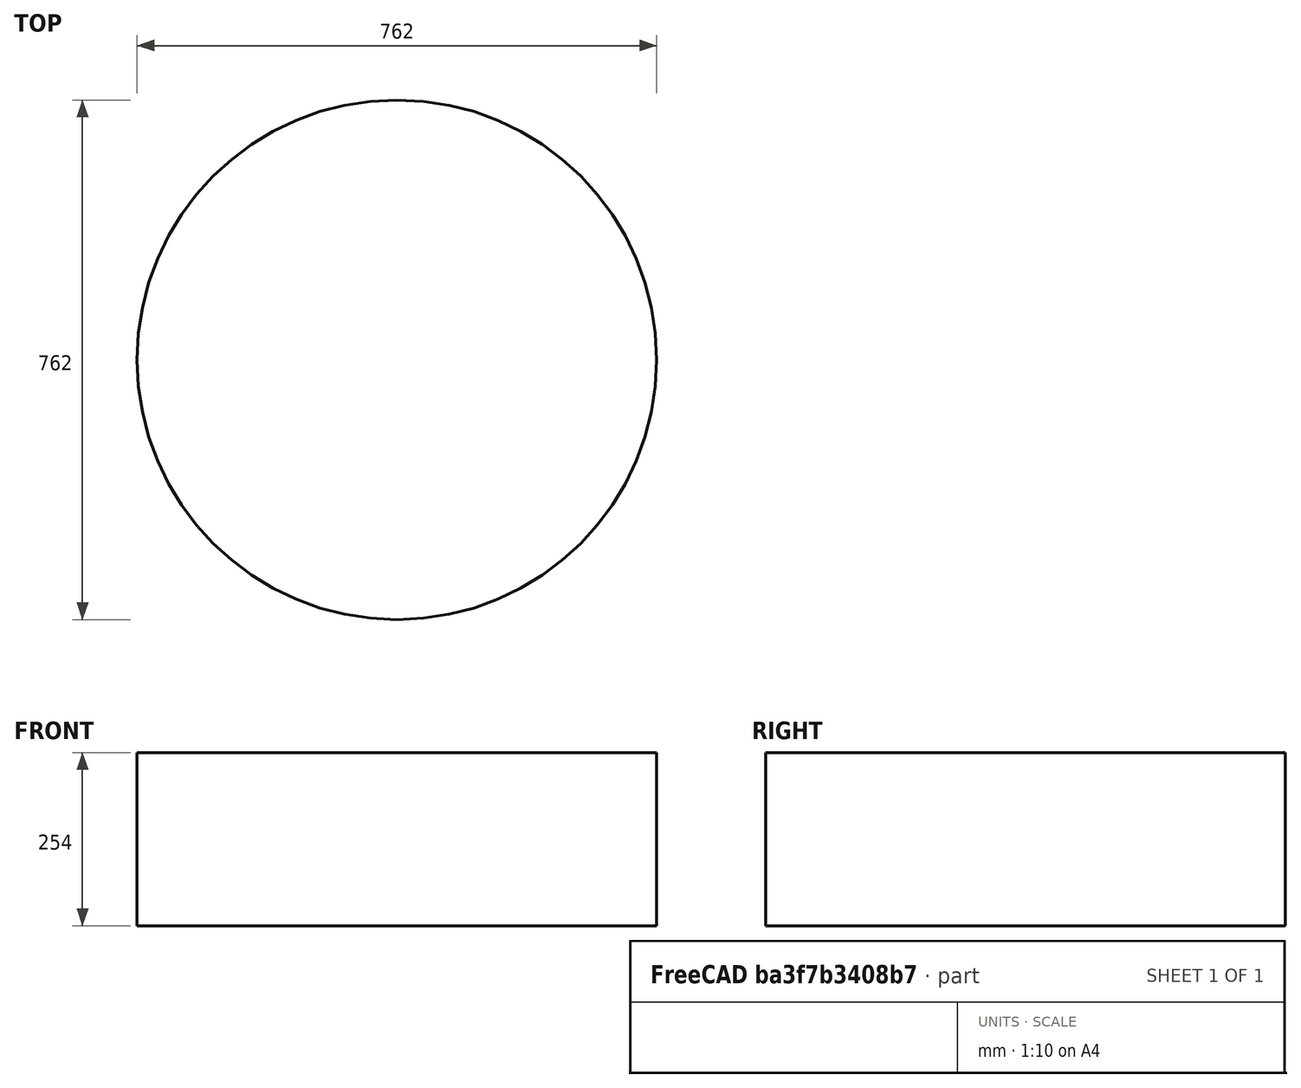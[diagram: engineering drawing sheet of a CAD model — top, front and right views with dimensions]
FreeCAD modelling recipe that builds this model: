
FCSTD DOCUMENT  (FreeCAD 1.0R39319 (Git))
Label: Cylinder-VarSet-Example
License: All rights reserved
LicenseURL: https://en.wikipedia.org/wiki/All_rights_reserved
objects: App::VarSet×2, Part::Cylinder×1
note: 1 computed .brp shape members not serialized (recipe doc carries the construction recipe); baked Part::Feature solids carry a one-line shape summary decoded from their .brp

FEATURE [Part::Cylinder] Cylinder
  Angle = 360
  AttacherType = Attacher::AttachEngine3D
  Base_Volume = 0
  FirstAngle = 0
  Height = 254
  Radius = 381
  SecondAngle = 0
  expr: Height = <<PQs>>.Base_Height
  expr: Radius = <<PQs>>.Base_Radius
FEATURE [App::VarSet] VarSet  label="PQs"
  Base_Density = 0.008
  Base_Dia = 762
  Base_Height = 254
  Base_Mass = 0
  Base_Radius = 381
  Base_Volume = 0
  CalcsLiveMappings = {\n  "docVersion": "0.2",\n  "unitsSchema": "UserPreferred",\n  "params": [],\n  "articles": [\n    {\n      "articleId": "3MA3D397Z-4DY",\n      "articleTitle": "Cylinder Container Sizing for Mass Calculation (freecad demo)",\n      "lastUpdated": "2025-10-28T05:19:12.139Z",\n      "paramMappings": {\n        "Base_Mass": {\n          "pqSymbol": "m",\n          "pqExpression": null,\n          "pqFaceValue": 1000,\n          "pqFaceUnit": "kg",\n          "pqBaseUnit": "kg"\n        },\n        "Base_Density": {\n          "pqSymbol": "rho",\n          "pqExpression": null,\n          "pqFaceValue": 50,\n          "pqFaceUnit": "lbm/ft\u00b3",\n          "pqBaseUnit": "kg/m\u00b3"\n        },\n        "Base_Height": {\n          "pqSymbol": "h",\n          "pqExpression": null,\n          "pqFaceValue": 12,\n          "pqFaceUnit": "in",\n          "pqBaseUnit": "m"\n        }\n      }\n    }\n  ]\n}
  expr: Base_Radius = Base_Dia / 2
FEATURE [App::VarSet] VarSet001  label="VS1"
  Base_x = 50.8
